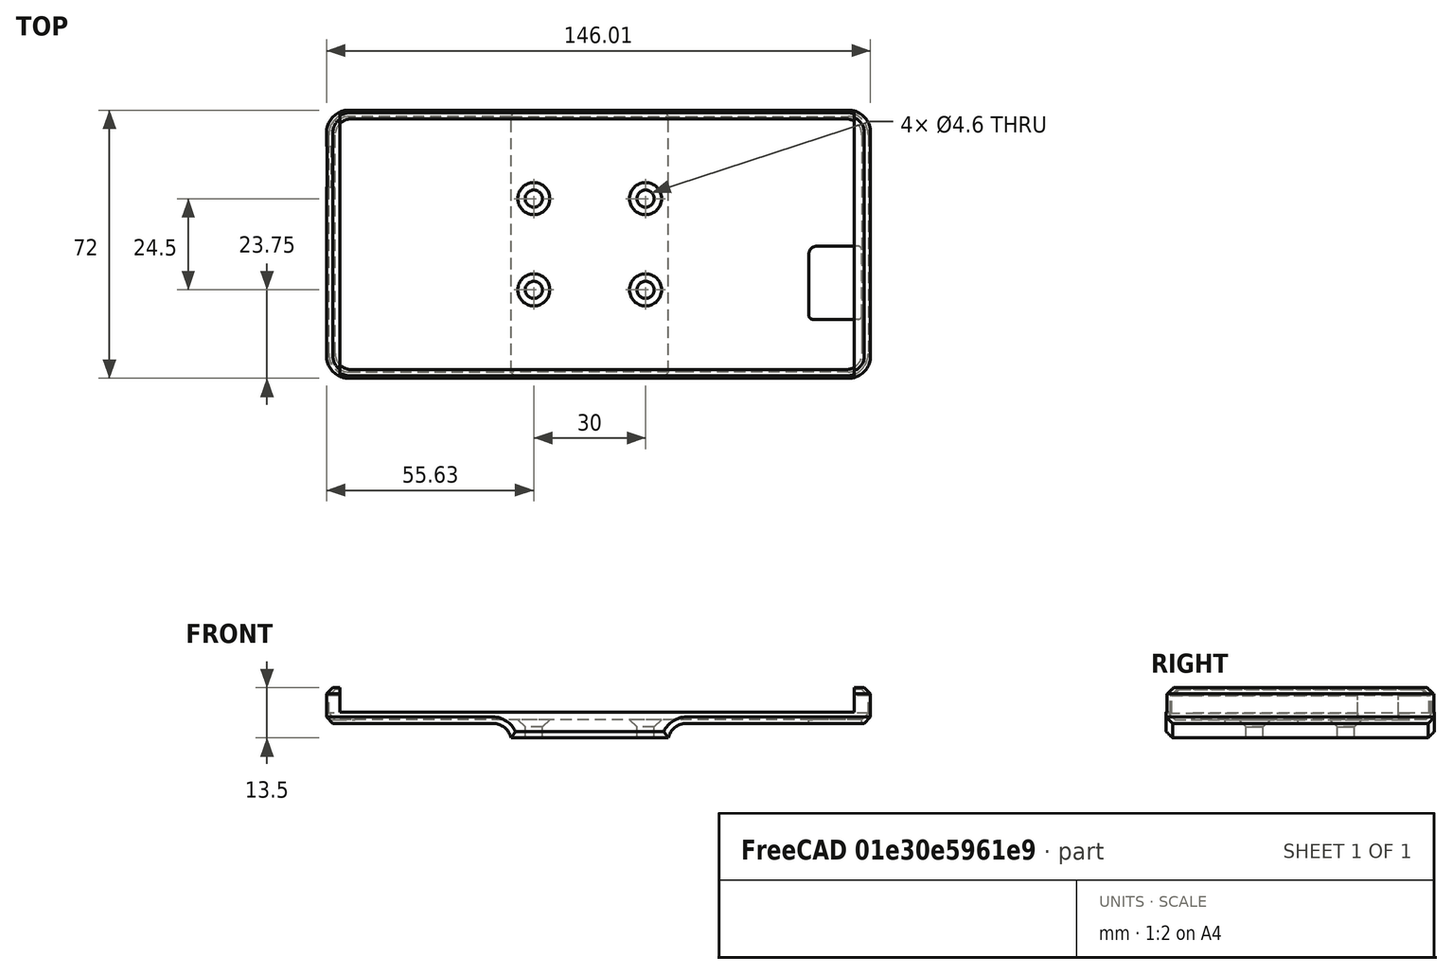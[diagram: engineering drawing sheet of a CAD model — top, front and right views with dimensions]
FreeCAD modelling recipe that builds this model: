
FCSTD DOCUMENT  (FreeCAD 0.16R5218 (Git))
Label: support_wiko_smart-roadster
License: All rights reserved
LicenseURL: http://en.wikipedia.org/wiki/All_rights_reserved
objects: Part::Box×7, Part::Cut×7, Part::Fillet×5, Part::Chamfer×5, Part::Cylinder×4, Part::Fuse×3
note: 31 computed .brp shape members not serialized (recipe doc carries the construction recipe); baked Part::Feature solids carry a one-line shape summary decoded from their .brp

FEATURE [Part::Box] Box  label="Base_Highway_4G"
  Height = 8.1
  Length = 144.75
  Width = 70.7
FEATURE [Part::Box] Box001  label="Base_boitier"
  Height = 13.5
  Length = 146
  Placement = pos=(-0.625,-0.65,-4.9) rot=(0,0,1;0rad)
  Width = 72
FEATURE [Part::Fillet] Fillet  label="W_Rayon_6"
  Base = -> Box
  Edges = 4 edges r=6: [Edge1,Edge3,Edge5,Edge7]
FEATURE [Part::Fillet] Fillet001  label="B_Rayon_6"
  Base = -> Box001
  Edges = 4 edges r=6: [Edge1,Edge3,Edge5,Edge7]
FEATURE [Part::Chamfer] Chamfer  label="W_Chanf_1,7"
  Base = -> Fillet
  Edges = 2 edges r=1.7: [Edge1,Edge4]
FEATURE [Part::Cut] Cut  label="Boitier_trouée_wiko"
  Base = -> Fillet001
  Tool = -> Chamfer
FEATURE [Part::Box] Box002  label="Cube_trou_ouverture_supérieure"
  Height = 10
  Length = 138
  Placement = pos=(3,-4,2) rot=(0,0,1;0rad)
  Width = 80
FEATURE [Part::Cut] Cut001  label="Boitier_ouvert"
  Base = -> Cut
  Tool = -> Box002
FEATURE [Part::Chamfer] Chamfer001  label="Boitier_ouvert_chanf"
  Base = -> Cut001
  Edges = 3 edges r=1.7: [Edge1,Edge4,Edge48]
FEATURE [Part::Cylinder] Cylinder  label="Trou_fixation_1"
  Angle = 360
  Height = 15
  Placement = pos=(0,0,-7) rot=(0,0,1;0rad)
  Radius = 2.3
FEATURE [Part::Cylinder] Cylinder001  label="Trou_fixation_2"
  Angle = 360
  Height = 15
  Placement = pos=(0,24.5,-7) rot=(0,0,1;0rad)
  Radius = 2.3
FEATURE [Part::Cylinder] Cylinder002  label="Trou_fixation_3"
  Angle = 360
  Height = 15
  Placement = pos=(30,24.5,-7) rot=(0,0,1;0rad)
  Radius = 2.3
FEATURE [Part::Cylinder] Cylinder003  label="Trou_fixation_4"
  Angle = 360
  Height = 15
  Placement = pos=(30,0,-7) rot=(0,0,1;0rad)
  Radius = 2.3
FEATURE [Part::Fuse] Fusion
  Base = -> Cylinder
  Tool = -> Cylinder001
FEATURE [Part::Fuse] Fusion001
  Base = -> Fusion
  Tool = -> Cylinder002
FEATURE [Part::Fuse] Fusion002  label="Bloc_des_trous"
  Base = -> Fusion001
  Placement = pos=(55,23.1,0) rot=(0,0,1;0rad)
  Tool = -> Cylinder003
FEATURE [Part::Cut] Cut002  label="Boitier_percé_fix"
  Base = -> Chamfer001
  Tool = -> Fusion002
FEATURE [Part::Chamfer] Chamfer002  label="Boitier_percé_fix_chanf"
  Base = -> Cut002
  Edges = 4 edges r=2: [Edge99,Edge101,Edge103,Edge105]
FEATURE [Part::Box] Box003  label="Evidement_inf_1"
  Height = 10
  Length = 50
  Placement = pos=(-1,-6,-11) rot=(0,0,1;0rad)
  Width = 80
FEATURE [Part::Box] Box004  label="Evidement_inf_2"
  Height = 10
  Length = 55
  Placement = pos=(91,-6,-11) rot=(0,0,1;0rad)
  Width = 80
FEATURE [Part::Fillet] Fillet002  label="Evidement_inf_1_arrondi"
  Base = -> Box003
  Edges = 1 edges r=5: [Edge6]
FEATURE [Part::Fillet] Fillet003  label="Evidement_inf_2_arrondi"
  Base = -> Box004
  Edges = 1 edges r=5: [Edge2]
FEATURE [Part::Cut] Cut003
  Base = -> Chamfer002
  Tool = -> Fillet002
FEATURE [Part::Cut] Cut004  label="Boitier_évidé_inf"
  Base = -> Cut003
  Tool = -> Fillet003
FEATURE [Part::Chamfer] Chamfer003
  Base = -> Cut004
  Edges = 1 edges r=1.7: [Edge72]
FEATURE [Part::Chamfer] Chamfer004  label="Boitié_évidé_inf_chanf"
  Base = -> Chamfer003
  Edges = 1 edges r=1.7: [Edge75]
FEATURE [Part::Box] Box005  label="Trou_USB"
  Height = 7
  Length = 10
  Placement = pos=(-3,50.7,0) rot=(0,0,1;0rad)
  Width = 11
FEATURE [Part::Cut] Cut005  label="Boitier"
  Base = -> Chamfer004
  Tool = -> Box005
FEATURE [Part::Box] Box006  label="Trou_objectif_photo"
  Height = 10
  Length = 14.2
  Placement = pos=(128.85,15.2,-5) rot=(0,0,1;0rad)
  Width = 19.6
FEATURE [Part::Fillet] Fillet004  label="Trou_obj_photo_congés"
  Base = -> Box006
  Edges = 4 edges: [Edge1 r=1,Edge3 r=2,Edge5 r=1,Edge7 r=1]
FEATURE [Part::Cut] Cut006  label="Boitier_obj_photo"
  Base = -> Cut005
  Tool = -> Fillet004
